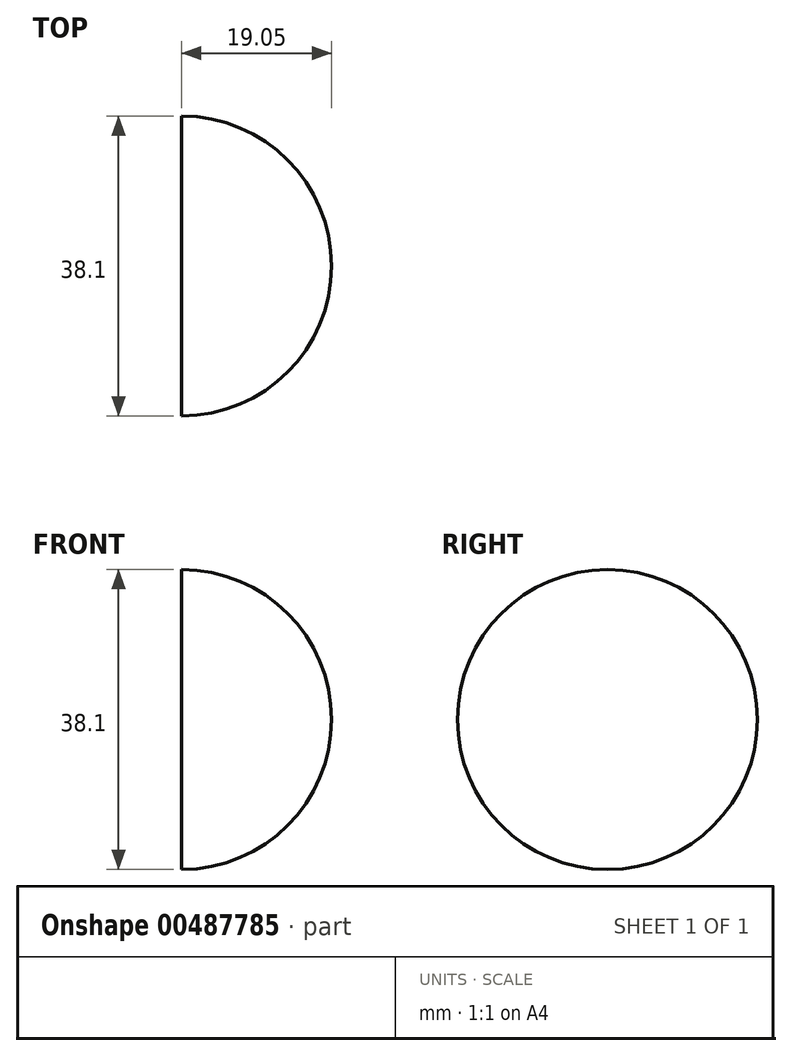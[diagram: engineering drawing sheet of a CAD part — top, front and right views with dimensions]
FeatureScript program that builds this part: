
annotation { "Feature Type Name" : "Feature", "Feature Type Description" : "" }
export const myFeature = defineFeature(function(context is Context, id is Id, definition is map)
    precondition{}
    {
        {
            var Q0;
            Q0=qCreatedBy(makeId("Front.planeOp"),FACE);
            var sketch = newSketch(context, id + "F0", { "sketchPlane" : qUnion([Q0])});
            skArc(sketch, "E0", {"start": v(0, -19.05) * mm, "mid": v(19.05, 0) * mm, "end": v(0, 19.05) * mm});
            skLineSegment(sketch, "E1", {"start": v(0, 19.05) * mm, "end": v(0, -19.05) * mm});
            skLineSegment(sketch, "E2", {"start": v(0, 0) * mm, "end": v(0, 57.05) * mm, "construction": true});
            skSolve(sketch);
        }
        {
            var Q0;
            Q0=makeQuery(id+"F0.imprint","IMPRINT",FACE,{"disambiguationData":[TD([[makeQuery(id+"F0.imprint","IMPRINT",EDGE,{"derivedFrom":sQuery(id+"F0.wireOp",EDGE,"E0")}),1.0]])]});
            var Q1;
            Q1=sQuery(id+"F0.wireOp",EDGE,"E2");
            revolve(context, id + "F1", {"entities" : qUnion([Q0]), "axis" : qUnion([Q1]), "revolveType" : RevolveType.SYMMETRIC, "angle" : 180 * degree});
        }
    });
